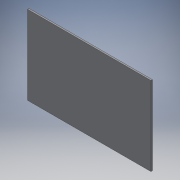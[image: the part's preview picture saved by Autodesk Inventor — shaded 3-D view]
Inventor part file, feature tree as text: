
AUTODESK INVENTOR PART (.ipt)
format: ipt  version: 2019 (Build 230136000, 136)  size: 331,264 bytes
history: native  units: mm
features: extrude x3, sketch x3, fillet x1
ambient origin geometry x8: Origin, YZ Plane, XZ Plane, XY Plane, X Axis, Y Axis, Z Axis, Center Point
bodies: Solid1 (feature_tree)
feature tree (7):
  extrude  "Extrusion1"  Depth=160.0mm
  extrude  "Extrusion2"  Depth=5.0mm
  fillet  "Fillet1"  Radius=5.0mm
  extrude  "Extrusion3"  Depth=10.0mm
  sketch  "Sketch1"  dims[d0=265.0mm d1=160.0mm]
  sketch  "Sketch2"  dims[d2=3.0mm d3=0.0mm d4=5.0mm d5=5.0mm]
  sketch  "Sketch3"  dims[d6=10.0mm d7=10.0mm d8=10.0mm d9=20.0mm d10=60.0mm d11=5.0mm d12=5.0mm d13=60.0mm d14=50.0mm d15=130.0mm d17=20.0mm d18=10.0mm d20=10.0mm d22=3.0mm d23=0.0mm d24=5.0mm d25=30.0mm d26=3.0mm d27=0.0mm]
